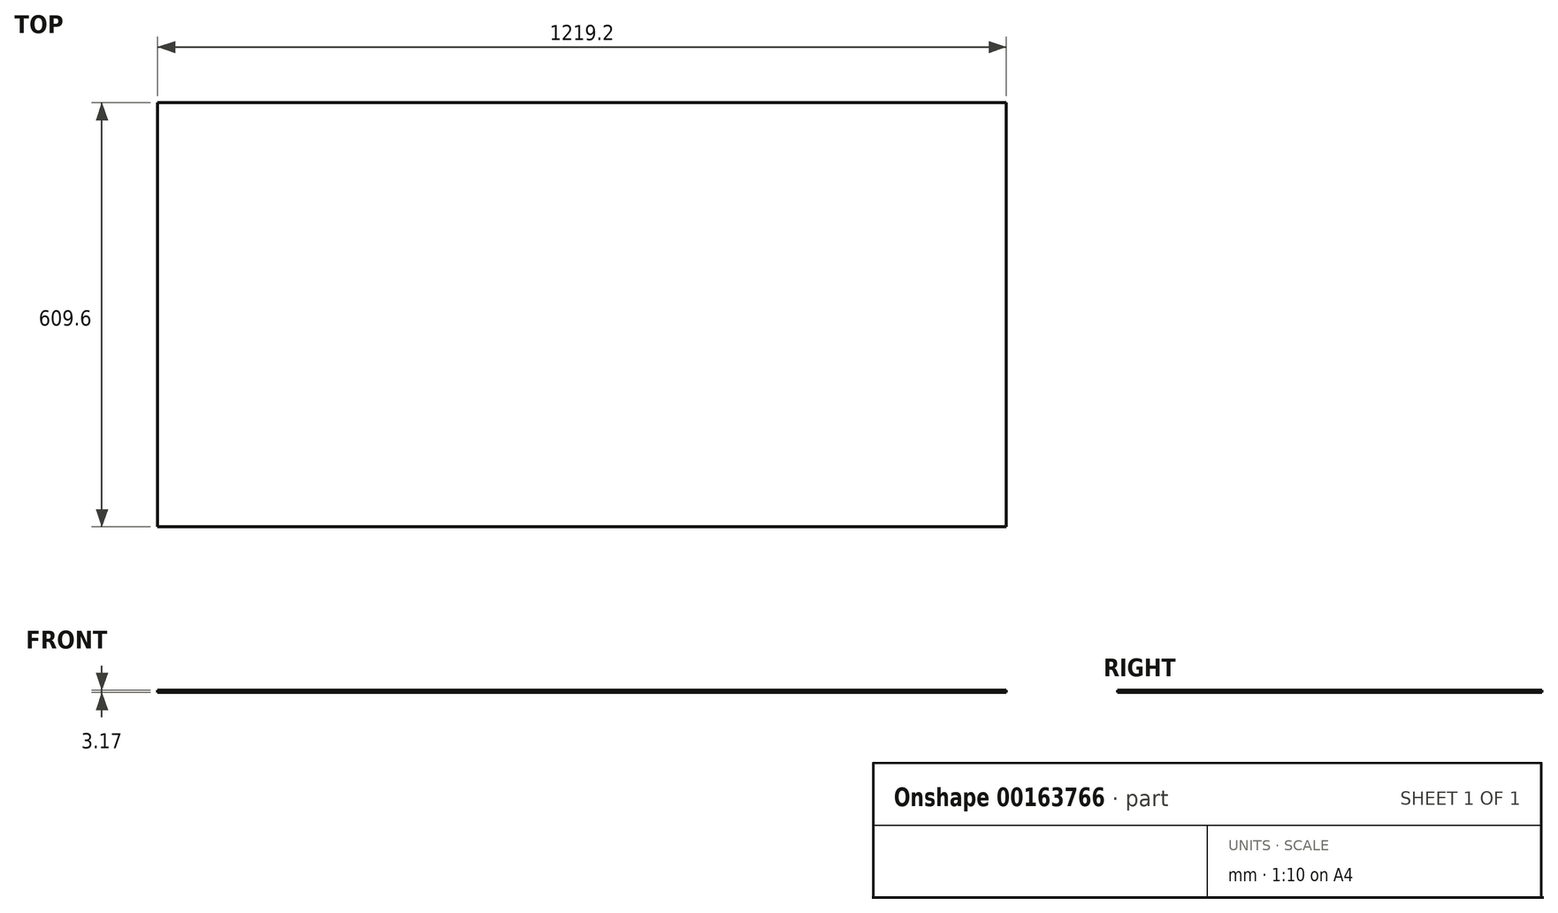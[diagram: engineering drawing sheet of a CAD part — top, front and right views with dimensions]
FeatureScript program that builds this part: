
annotation { "Feature Type Name" : "Feature", "Feature Type Description" : "" }
export const myFeature = defineFeature(function(context is Context, id is Id, definition is map)
    precondition{}
    {
        {
            var Q0;
            Q0=qCreatedBy(makeId("Top.planeOp"),FACE);
            var sketch = newSketch(context, id + "F0", { "sketchPlane" : qUnion([Q0])});
            skLineSegment(sketch, "E0.bottom", {"start": v(609.6, 304.8) * mm, "end": v(-609.6, 304.8) * mm});
            skLineSegment(sketch, "E0.top", {"start": v(609.6, -304.8) * mm, "end": v(-609.6, -304.8) * mm});
            skLineSegment(sketch, "E0.left", {"start": v(609.6, 304.8) * mm, "end": v(609.6, -304.8) * mm});
            skLineSegment(sketch, "E0.right", {"start": v(-609.6, 304.8) * mm, "end": v(-609.6, -304.8) * mm});
            skPoint(sketch, "E0.middle", {"position": v(0, 0) * mm});
            skSolve(sketch);
        }
        {
            var Q0;
            Q0 = qSketchRegion(id + "F0", true);
            extrude(context, id + "F1", {"entities" : qUnion([Q0]), "depth" : 3.17 * mm});
        }
    });
